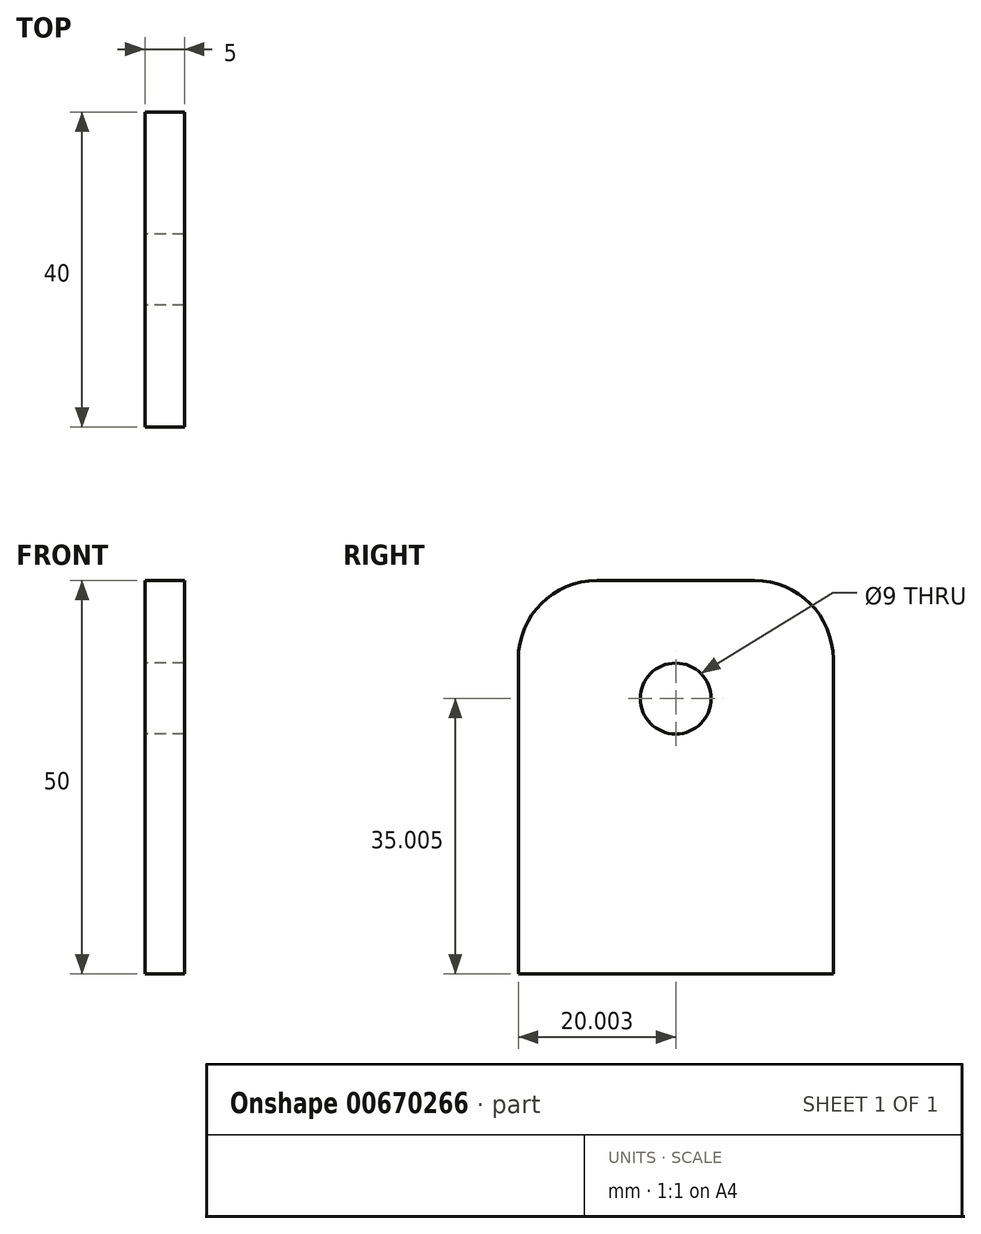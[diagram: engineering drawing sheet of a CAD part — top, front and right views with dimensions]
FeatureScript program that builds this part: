
annotation { "Feature Type Name" : "Feature", "Feature Type Description" : "" }
export const myFeature = defineFeature(function(context is Context, id is Id, definition is map)
    precondition{}
    {
        {
            var Q0;
            Q0=qCreatedBy(makeId("Right.planeOp"),FACE);
            var sketch = newSketch(context, id + "F0", { "sketchPlane" : qUnion([Q0])});
            skLineSegment(sketch, "E0.bottom", {"start": v(-8.27, 34.44) * mm, "end": v(11.73, 34.44) * mm});
            skLineSegment(sketch, "E0.top", {"start": v(-18.27, -15.56) * mm, "end": v(21.73, -15.56) * mm});
            skLineSegment(sketch, "E0.left", {"start": v(-18.27, 24.44) * mm, "end": v(-18.27, -15.56) * mm});
            skLineSegment(sketch, "E0.right", {"start": v(21.73, 24.44) * mm, "end": v(21.73, -15.56) * mm});
            skPoint(sketch, "E1.visualSharp", {"position": v(-18.27, 34.44) * mm});
            skArc(sketch, "E1.filletArc", {"start": v(-8.27, 34.44) * mm, "mid": v(-15.34, 31.52) * mm, "end": v(-18.27, 24.44) * mm});
            skPoint(sketch, "E2.visualSharp", {"position": v(21.73, 34.44) * mm});
            skArc(sketch, "E2.filletArc", {"start": v(21.73, 24.44) * mm, "mid": v(18.8, 31.52) * mm, "end": v(11.73, 34.44) * mm});
            skCircle(sketch, "E3", {"center": v(1.73, 19.44) * mm, "radius": 4.5 * mm});
            skSolve(sketch);
        }
        {
            var Q0;
            Q0=makeQuery(id+"F0.imprint","IMPRINT",FACE,{"disambiguationData":[TD([[makeQuery(id+"F0.imprint","IMPRINT",EDGE,{"derivedFrom":sQuery(id+"F0.wireOp",EDGE,"E0.bottom")}),-1.0]])]});
            extrude(context, id + "F1", {"entities" : qUnion([Q0]), "depth" : 5 * mm, "offsetDistance" : 25 * mm});
        }
    });
